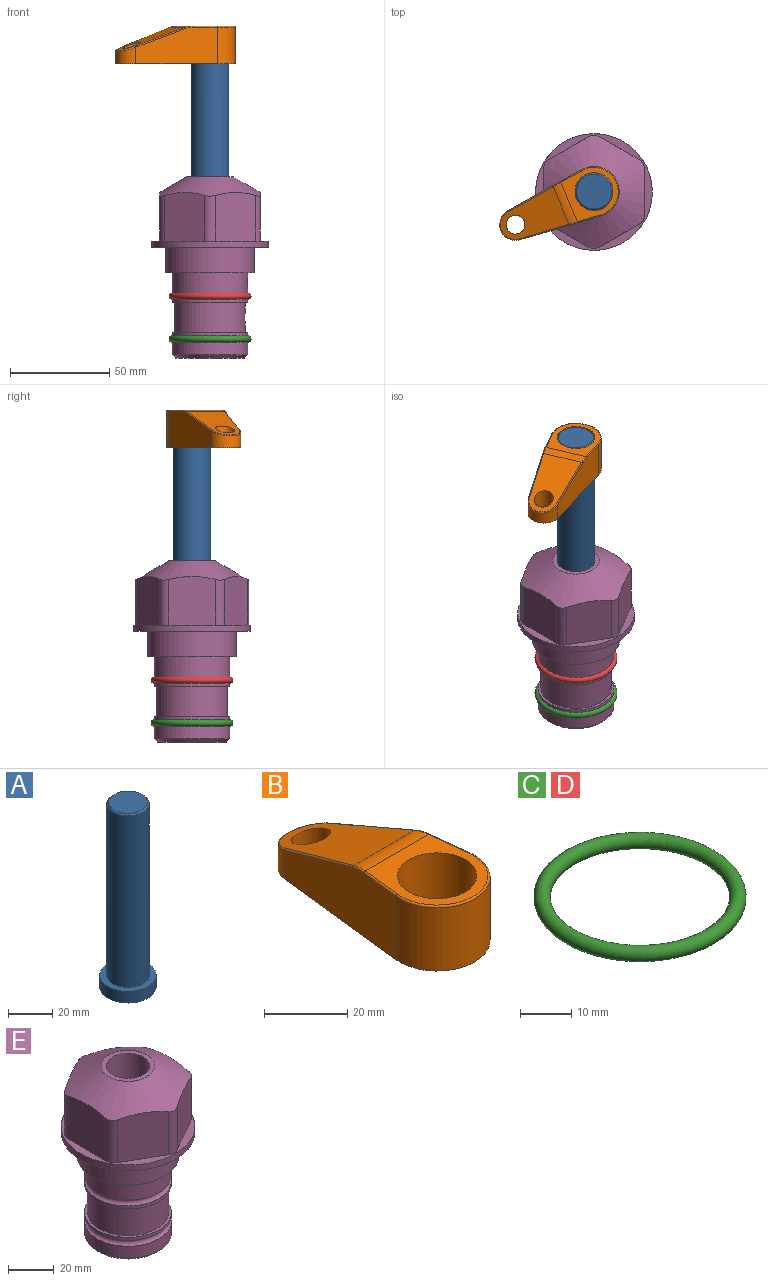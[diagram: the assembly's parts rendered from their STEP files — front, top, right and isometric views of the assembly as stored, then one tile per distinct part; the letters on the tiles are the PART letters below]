
ASSEMBLY  parts=5 mates=3
PART A: 6 faces, bbox 25.4x25.4x101.6 mm
  f0: plane 17.46x17.46mm, normal (0,0,1), area 239.5mm2, adj f5
  f1: plane 25.4x25.4mm, normal (0,0,-1), area 506.7mm2, adj f2
  f2: cylinder r=12.7mm len=25.4mm, axis (0,0,1), area 506.7mm2, adj f1,f3
  f3: plane 25.4x25.4mm, normal (0,0,1), area 221.7mm2, adj f2,f4
  f4: cylinder r=9.53mm len=94.46mm, axis (0,0,1), area 5653mm2, adj f3,f5
  f5: cone r=8.73mm half-angle=45deg, axis (0,0,-1), area 64.4mm2, adj f0,f4
PART B: 44 faces, bbox 27.5x64.5x19.1 mm
  f0: plane 2.3x0.95mm, normal (0,0,-1), area 1mm2, adj f25,f30,f34
  f1: plane 63.5x25.4mm, normal (0,0,-1), area 561.7mm2, adj f2,f3,f4,f5,f6,f7,f19,f20
  f2: cylinder r=12.7mm len=25.4mm, axis (0,0,-1), area 792.2mm2, adj f1,f3,f5,f13
  f3: plane 42.33x18.54mm, normal (0.99,0.11,0), area 647mm2, adj f1,f2,f4,f11,f12,f14
  f4: cylinder r=7.94mm len=15.78mm, axis (0,0,-1), area 158.6mm2, adj f1,f3,f5,f16
  f5: plane 42.33x18.54mm, normal (-0.99,0.11,0), area 647mm2, adj f1,f2,f4,f15,f17,f18
  f6: cylinder r=9.53mm len=19.05mm, axis (0,0,-1), area 1140.1mm2, adj f1,f8
  f7: cylinder r=4.76mm len=10.98mm, axis (0,0,-1), area 276.1mm2, adj f1,f9
  f8: plane 25.83x24.38mm, normal (0,0,1), area 262.2mm2, adj f6,f10,f11,f13,f15
  f9: plane 32.49x20.55mm, normal (0,0.34,0.94), area 489.9mm2, adj f7,f10,f14,f16,f18
  f10: cylinder r=12.7mm len=21.49mm, axis (-1,0,0), area 93.2mm2, adj f8,f9,f12,f17
  f11: cylinder r=0.51mm len=12.34mm, axis (0.11,-0.99,0), area 9.9mm2, adj f3,f8,f12,f13
  f12: bspline ~7.62x1.64mm, area 3.5mm2, adj f3,f10,f11,f14
  f13: torus R=12.19mm, axis (0,0,1), area 33.6mm2, adj f2,f8,f11,f15
  f14: cylinder r=0.51mm len=26.01mm, axis (0.1,-0.93,0.34), area 21.6mm2, adj f3,f9,f12,f16
  f15: cylinder r=0.51mm len=12.34mm, axis (0.11,0.99,0), area 9.9mm2, adj f5,f8,f13,f17
  f16: bspline ~15.78x7.05mm, area 15.7mm2, adj f4,f9,f14,f18
  f17: bspline ~7.62x1.64mm, area 3.5mm2, adj f5,f10,f15,f18
  f18: cylinder r=0.51mm len=26.01mm, axis (0.1,0.93,-0.34), area 21.6mm2, adj f5,f9,f16,f17
  f19: plane 21.6x14.29mm, normal (-0.99,-0.11,0), area 242.6mm2, adj f1,f26,f28,f34,f36,f38
  f20: plane 21.6x14.29mm, normal (0.99,-0.11,0), area 242.6mm2, adj f1,f27,f29,f37,f39,f41
  f21: cylinder r=12.7mm len=14.29mm, axis (0,0,-1), area 173.2mm2, adj f1,f26,f27,f30,f31,f33
  f22: cylinder r=7.94mm len=7.63mm, axis (0,0,-1), area 53.8mm2, adj f1,f28,f29,f42
  f23: plane 2.3x0.95mm, normal (0,0,-1), area 1mm2, adj f25,f33,f37
  f24: plane 17.94x12.32mm, normal (0,-0.34,-0.94), area 191.2mm2, adj f25,f38,f41,f42
  f25: cylinder r=9.53mm len=12.93mm, axis (-1,0,0), area 37.5mm2, adj f0,f23,f24,f31,f36,f39
  f26: cylinder r=1.59mm len=14.29mm, axis (0,0,-1), area 49mm2, adj f1,f19,f21,f32
  f27: cylinder r=1.59mm len=14.29mm, axis (0,0,-1), area 49mm2, adj f1,f20,f21,f35
  f28: cylinder r=1.59mm len=7.28mm, axis (0,0,-1), area 22.1mm2, adj f1,f19,f22,f40
  f29: cylinder r=1.59mm len=7.28mm, axis (0,0,-1), area 22.1mm2, adj f1,f20,f22,f43
  f30: torus R=14.29mm, axis (0,0,1), area 5.8mm2, adj f0,f21,f31,f32
  f31: bspline ~11.06x2.73mm, area 20.8mm2, adj f21,f25,f30,f33
  f32: sphere r=1.59mm, area 5.4mm2, adj f26,f30,f34
  f33: torus R=14.29mm, axis (0,0,1), area 5.8mm2, adj f21,f23,f31,f35
  f34: cylinder r=1.59mm len=1.68mm, axis (-0.11,0.99,0), area 2.4mm2, adj f0,f19,f32,f36
  f35: sphere r=1.59mm, area 5.4mm2, adj f27,f33,f37
  f36: bspline ~5.82x2.33mm, area 7.7mm2, adj f19,f25,f34,f38
  f37: cylinder r=1.59mm len=1.68mm, axis (0.11,0.99,0), area 2.4mm2, adj f20,f23,f35,f39
  f38: cylinder r=1.59mm len=18.33mm, axis (0.1,-0.93,0.34), area 46.7mm2, adj f19,f24,f36,f40
  f39: bspline ~5.82x2.33mm, area 7.7mm2, adj f20,f25,f37,f41
  f40: sphere r=1.59mm, area 3.6mm2, adj f28,f38,f42
  f41: cylinder r=1.59mm len=18.33mm, axis (0.1,0.93,-0.34), area 46.7mm2, adj f20,f24,f39,f43
  f42: bspline ~8.31x1.84mm, area 15.3mm2, adj f22,f24,f40,f43
  f43: sphere r=1.59mm, area 3.6mm2, adj f29,f41,f42
PART C: 1 faces, bbox 44.7x44.7x3.2 mm
  f0: torus R=19.05mm, axis (0,0,1), area 1193.9mm2
PART D: same geometry as C
PART E: 36 faces, bbox 58.7x58.7x91.2 mm
  f0: cylinder r=17.78mm len=35.56mm, axis (0,0,1), area 1670.8mm2, adj f23,f24,f31
  f1: cylinder r=19.05mm len=38.1mm, axis (0,0,1), area 1191.9mm2, adj f26,f27,f30
  f2: plane 58.66x58.66mm, normal (0,0,-1), area 1150.6mm2, adj f3,f28
  f3: cylinder r=29.33mm len=58.66mm, axis (0,0,-1), area 585.1mm2, adj f2,f4
  f4: plane 58.66x58.66mm, normal (0,0,1), area 475.9mm2, adj f3,f5,f6,f7,f8,f9,f10,f11
  f5: plane 24.5x20.32mm, normal (-0.5,0.87,0), area 562.8mm2, adj f4,f15,f16,f17
  f6: plane 24.5x20.32mm, normal (0.5,0.87,0), area 562.8mm2, adj f4,f14,f15,f17
  f7: plane 24.5x23.48mm, normal (1,0,0), area 562.8mm2, adj f4,f13,f14,f17
  f8: plane 24.5x20.32mm, normal (0.5,-0.87,0), area 562.8mm2, adj f4,f12,f13,f17
  f9: plane 24.5x20.32mm, normal (-0.5,-0.87,0), area 562.8mm2, adj f4,f11,f12,f17
  f10: plane 24.5x23.48mm, normal (-1,0,0), area 562.8mm2, adj f4,f11,f16,f17
  f11: cylinder r=5.08mm len=23.01mm, axis (0,0,-1), area 121.2mm2, adj f4,f9,f10,f17
  f12: cylinder r=5.08mm len=23.01mm, axis (0,0,-1), area 121.2mm2, adj f4,f8,f9,f17
  f13: cylinder r=5.08mm len=23.01mm, axis (0,0,-1), area 121.2mm2, adj f4,f7,f8,f17
  f14: cylinder r=5.08mm len=23.01mm, axis (0,0,-1), area 121.2mm2, adj f4,f6,f7,f17
  f15: cylinder r=5.08mm len=23.01mm, axis (0,0,-1), area 121.2mm2, adj f4,f5,f6,f17
  f16: cylinder r=5.08mm len=23.01mm, axis (0,0,-1), area 121.2mm2, adj f4,f5,f10,f17
  f17: cone r=11.73mm half-angle=60deg, axis (0,0,-1), area 2071.8mm2, adj f5,f6,f7,f8,f9,f10,f11,f12
  f18: plane 23.46x23.46mm, normal (0,0,1), area 147.4mm2, adj f17,f35
  f19: plane 34.93x34.93mm, normal (0,0,-1), area 958mm2, adj f29
  f20: cylinder r=19.05mm len=38.1mm, axis (0,0,1), area 760.1mm2, adj f21,f29
  f21: torus R=19.05mm, axis (0,0,1), area 565.3mm2, adj f20,f22
  f22: cylinder r=19.05mm len=38.1mm, axis (0,0,1), area 190mm2, adj f21,f23
  f23: plane 38.1x38.1mm, normal (0,0,1), area 146.9mm2, adj f0,f22
  f24: plane 38.1x38.1mm, normal (0,0,-1), area 146.9mm2, adj f0,f25
  f25: cylinder r=19.05mm len=38.1mm, axis (0,0,1), area 190mm2, adj f24,f26
  f26: torus R=19.05mm, axis (0,0,1), area 565.3mm2, adj f1,f25
  f27: plane 44.45x44.45mm, normal (0,0,-1), area 411.7mm2, adj f1,f28
  f28: cylinder r=22.23mm len=44.45mm, axis (0,0,1), area 1773.5mm2, adj f2,f27
  f29: cone r=19.05mm half-angle=45deg, axis (0,0,1), area 257.5mm2, adj f19,f20
  f30: cylinder r=3.17mm len=6.75mm, axis (-1,0,0), area 128mm2, adj f1,f33
  f31: cylinder r=3.17mm len=6.35mm, axis (-1,0,0), area 102.5mm2, adj f0,f33
  f32: plane 25.4x25.4mm, normal (0,0,1), area 506.7mm2, adj f33
  f33: cylinder r=12.7mm len=66.42mm, axis (0,0,-1), area 5236.2mm2, adj f30,f31,f32,f34
  f34: cone r=9.53mm half-angle=30deg, axis (0,0,-1), area 443.4mm2, adj f33,f35
  f35: cylinder r=9.53mm len=19.05mm, axis (0,0,-1), area 849mm2, adj f18,f34
PLACE A rot(axis=(0,0,-1),157.2deg) t=(0,0,37.8)mm
PLACE B rot(axis=(0,0,1),112.8deg) t=(0,0,92.41)mm
PLACE C t=(0,0,-21.59)mm
PLACE D at identity
PLACE E at identity fixed
MATE fastened C.f0 <-> E.f0  axis (0,0,1) through (0,0,-46.1)mm
MATE cylindrical A.f2 <-> E.f0  axis (0,0,1) through (0,0,63.44)mm
MATE fastened B.f2 <-> A.f2  axis (0,0,1) through (0,0,111.46)mm
